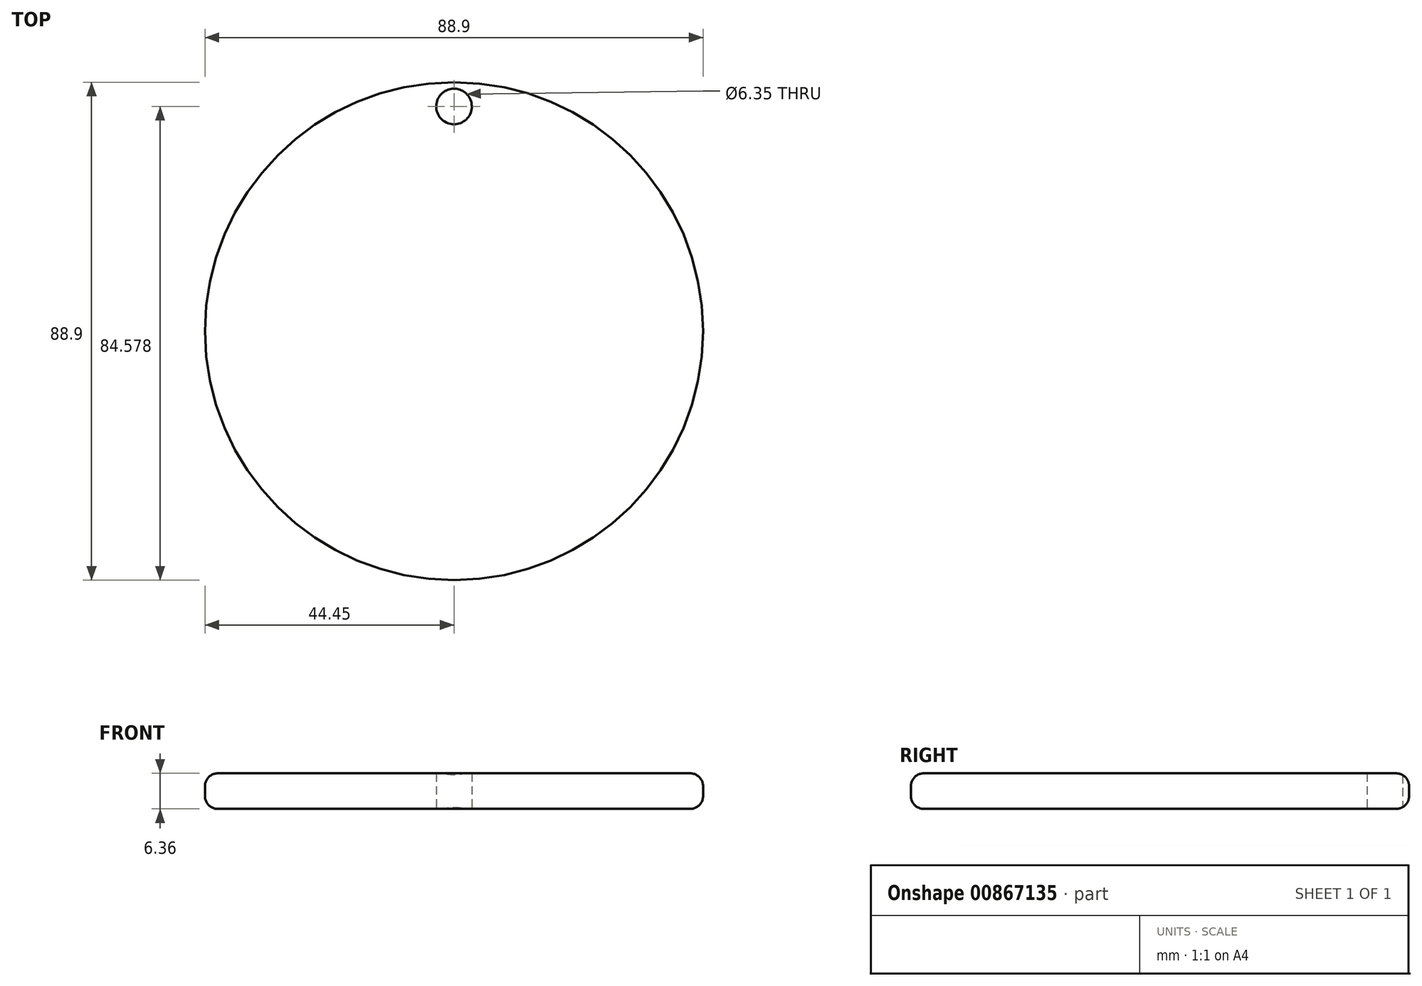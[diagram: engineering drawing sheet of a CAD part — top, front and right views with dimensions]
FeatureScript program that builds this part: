
annotation { "Feature Type Name" : "Feature", "Feature Type Description" : "" }
export const myFeature = defineFeature(function(context is Context, id is Id, definition is map)
    precondition{}
    {
        {
            var Q0;
            Q0=qCreatedBy(makeId("Top.planeOp"),FACE);
            var sketch = newSketch(context, id + "F0", { "sketchPlane" : qUnion([Q0])});
            skCircle(sketch, "E0", {"center": v(0, 0) * mm, "radius": 44.45 * mm});
            skSolve(sketch);
        }
        {
            var Q0;
            Q0 = qSketchRegion(id + "F0", true);
            extrude(context, id + "F1", {"entities" : qUnion([Q0]), "endBound" : BoundingType.SYMMETRIC, "depth" : 6.35 * mm, "offsetDistance" : 25.4 * mm});
        }
        {
            var Q0;
            Q0=qCreatedBy(makeId("Top.planeOp"),FACE);
            var sketch = newSketch(context, id + "F2", { "sketchPlane" : qUnion([Q0])});
            skCircle(sketch, "E1", {"center": v(0, 40.13) * mm, "radius": 3.18 * mm});
            skSolve(sketch);
        }
        {
            var Q0;
            Q0 = qSketchRegion(id + "F2", true);
            extrude(context, id + "F3", {"entities" : qUnion([Q0]), "operationType" : NewBodyOperationType.REMOVE, "endBound" : BoundingType.SYMMETRIC, "depth" : 25.4 * mm, "offsetDistance" : 25.4 * mm});
        }
        {
            var Q0;
            Q0=makeQuery(id+"F1.opExtrude","CAP_EDGE",EDGE,{"disambiguationData":[OSD([sQuery(id+"F0.wireOp",EDGE,"E0")])],"isStart":false});
            var Q1;
            Q1=makeQuery(id+"F1.opExtrude","CAP_EDGE",EDGE,{"disambiguationData":[OSD([sQuery(id+"F0.wireOp",EDGE,"E0")])],"isStart":true});
            fillet(context, id + "F4", {"entities" : qUnion([Q0, Q1]), "radius" : 2.3 * mm, "tangentPropagation" : true, "allowEdgeOverflow" : false});
        }
    });
